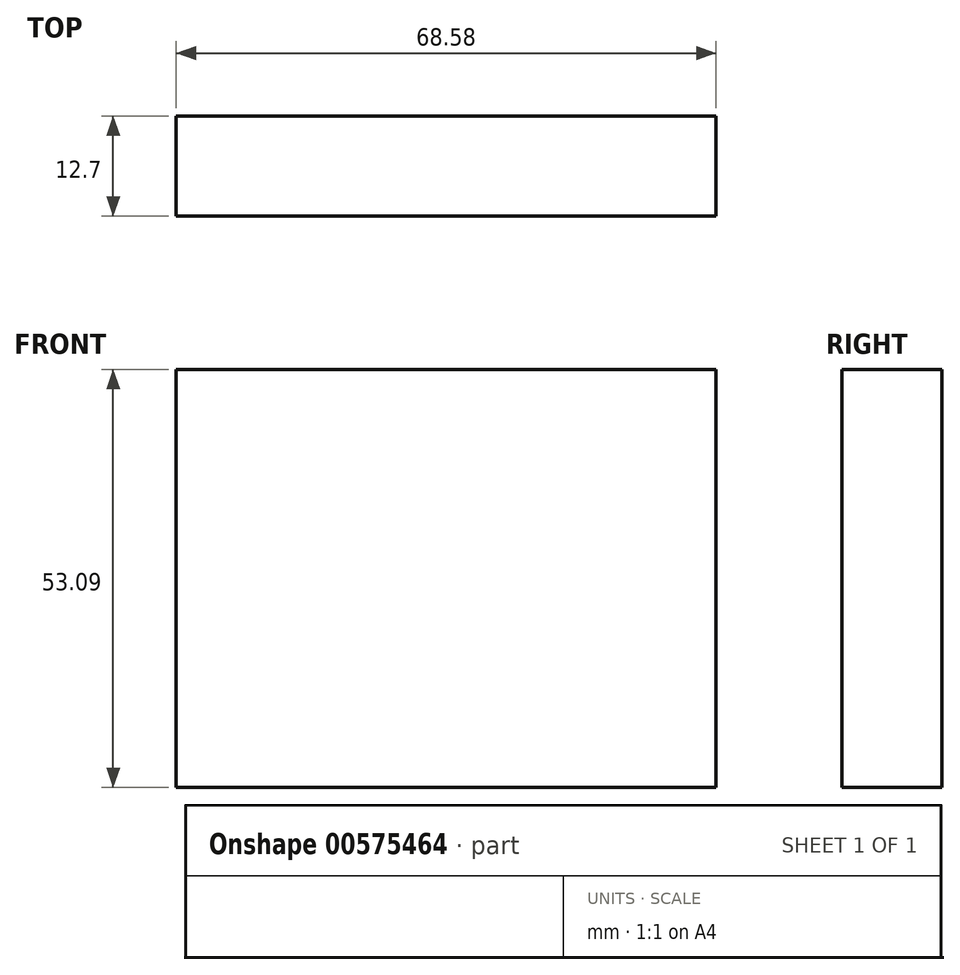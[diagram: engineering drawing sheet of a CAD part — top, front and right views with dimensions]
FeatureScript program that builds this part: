
annotation { "Feature Type Name" : "Feature", "Feature Type Description" : "" }
export const myFeature = defineFeature(function(context is Context, id is Id, definition is map)
    precondition{}
    {
        {
            var Q0;
            Q0=qCreatedBy(makeId("Front.planeOp"),FACE);
            var sketch = newSketch(context, id + "F0", { "sketchPlane" : qUnion([Q0])});
            skLineSegment(sketch, "E0.bottom", {"start": v(6.24, 31.42) * mm, "end": v(74.82, 31.42) * mm});
            skLineSegment(sketch, "E0.top", {"start": v(6.24, -21.67) * mm, "end": v(74.82, -21.67) * mm});
            skLineSegment(sketch, "E0.left", {"start": v(6.24, 31.42) * mm, "end": v(6.24, -21.67) * mm});
            skLineSegment(sketch, "E0.right", {"start": v(74.82, 31.42) * mm, "end": v(74.82, -21.67) * mm});
            skSolve(sketch);
        }
        {
            var Q0;
            Q0 = qSketchRegion(id + "F0", true);
            extrude(context, id + "F1", {"entities" : qUnion([Q0]), "depth" : 12.7 * mm, "offsetDistance" : 25.4 * mm});
        }
    });
